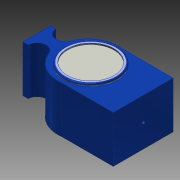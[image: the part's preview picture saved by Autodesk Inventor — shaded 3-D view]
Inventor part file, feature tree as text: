
AUTODESK INVENTOR PART (.ipt)
format: ipt  version: 2015 (Build 190159000, 159)  size: 135,168 bytes
history: native  units: in
note: dims shown in document units (in); Inventor stores cm internally (conversion verified against a paired STEP export)
features: extrude x3, sketch x2, hole x1, fillet x1
ambient origin geometry x8: Origin, YZ Plane, XZ Plane, XY Plane, X Axis, Y Axis, Z Axis, Center Point
bodies: Solid1 (feature_tree)
feature tree (7):
  extrude  "Extrusion1"  Depth=4.0in
  hole  "Hole1"  [1 undecoded]
  sketch  "Sketch2"  dims[d3=1.75in d4=0.0in d5=1.0in d6=1.0in d7=0.125in d8=0.75in d9=0.375in d10=0.25in d11=0.5635in d12=1.0in d13=0.8108in d14=2.0in d15=1.0in d18=1.75in d19=0.1in d20=0.0in d21=0.05in d22=0.0in d23=0.05in]
  extrude  "Extrusion3"  Depth=0.05in
  extrude  "Extrusion4"  Depth=1.0in
  fillet  "Fillet1"  Radius=1.75in
  sketch  "Sketch1"  dims[d1=2.25in d2=4.0in]
note: 1 required parameter value undecoded (feature->parameter linkage not recoverable at this tier; creation-order binding heuristic only, values carry confidence <= 0.55)
